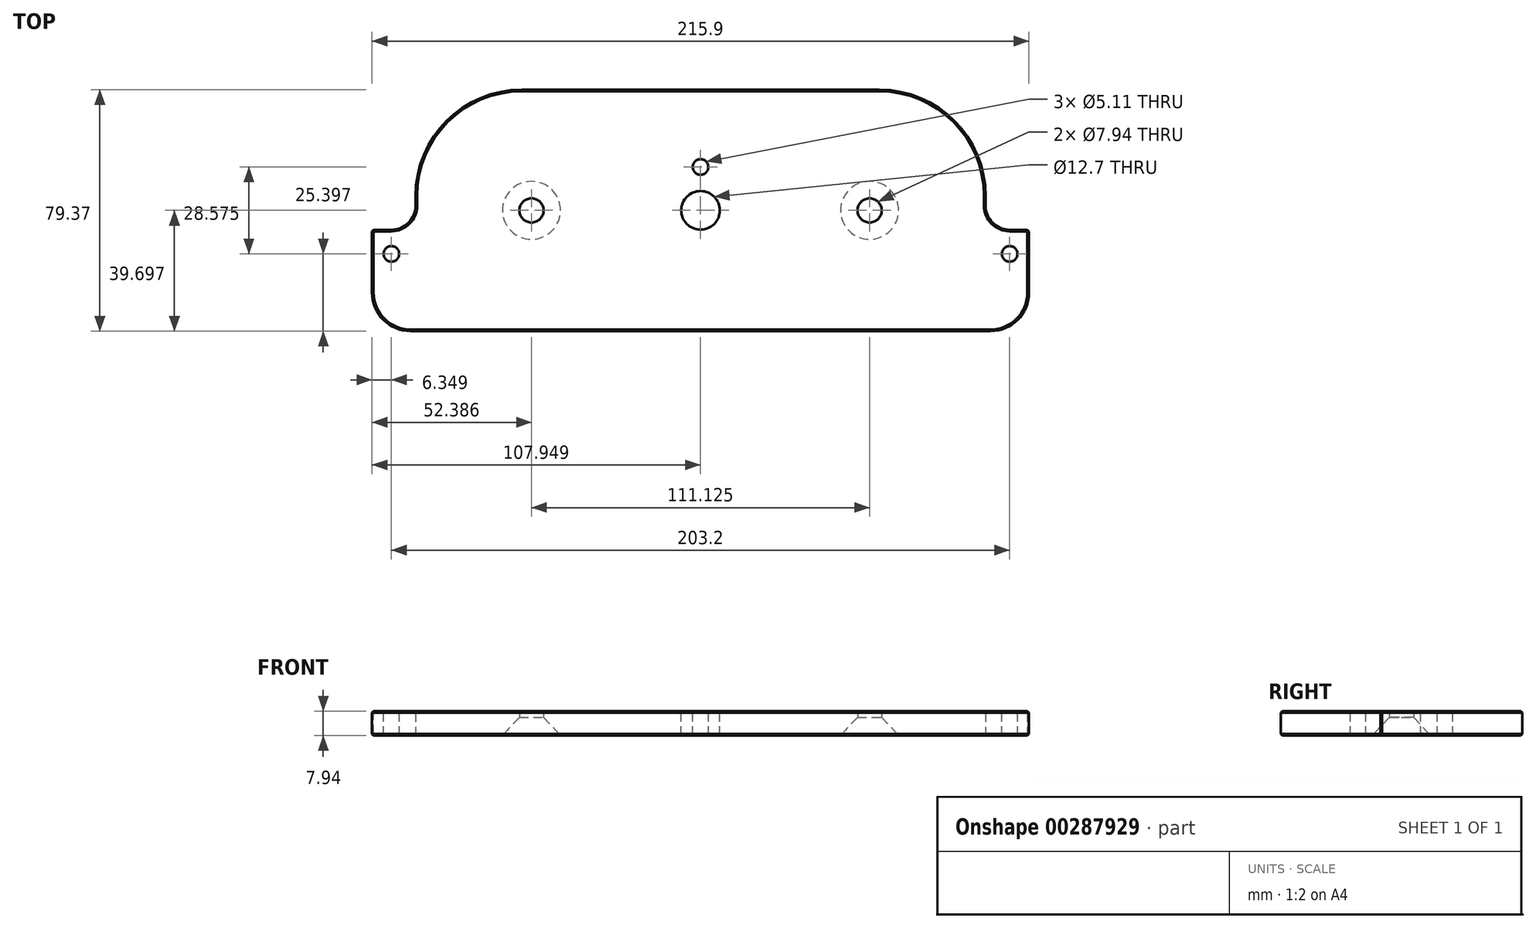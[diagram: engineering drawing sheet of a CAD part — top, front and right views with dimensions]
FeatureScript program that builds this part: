
annotation { "Feature Type Name" : "Feature", "Feature Type Description" : "" }
export const myFeature = defineFeature(function(context is Context, id is Id, definition is map)
    precondition{}
    {
        {
            var Q0;
            Q0=qCreatedBy(makeId("Top.planeOp"),FACE);
            var sketch = newSketch(context, id + "F0", { "sketchPlane" : qUnion([Q0])});
            skLineSegment(sketch, "E0.bottom", {"start": v(-112.58, 82.11) * mm, "end": v(103.32, 82.11) * mm});
            skLineSegment(sketch, "E0.top", {"start": v(-112.58, 2.74) * mm, "end": v(103.32, 2.74) * mm});
            skLineSegment(sketch, "E0.left", {"start": v(-112.58, 82.11) * mm, "end": v(-112.58, 2.74) * mm});
            skLineSegment(sketch, "E0.right", {"start": v(103.32, 82.11) * mm, "end": v(103.32, 2.74) * mm});
            skLineSegment(sketch, "E1", {"start": v(89.03, 82.11) * mm, "end": v(89.03, 36.07) * mm});
            skLineSegment(sketch, "E2", {"start": v(89.03, 36.07) * mm, "end": v(103.32, 36.07) * mm});
            skLineSegment(sketch, "E3", {"start": v(-112.58, 36.07) * mm, "end": v(-98.3, 36.07) * mm});
            skLineSegment(sketch, "E4", {"start": v(-98.3, 36.07) * mm, "end": v(-98.3, 82.11) * mm});
            skSolve(sketch);
        }
        {
            var Q0;
            {var subQ1=sQuery(id+"F0.wireOp",EDGE,"E0.top");Q0=makeQuery(id+"F0.imprint","IMPRINT",FACE,{"disambiguationData":[TD([[makeQuery(id+"F0.imprint","IMPRINT",EDGE,{"derivedFrom":subQ1}),1.0]])]});}
            extrude(context, id + "F1", {"entities" : qUnion([Q0]), "depth" : 7.94 * mm, "offsetDistance" : 25.4 * mm});
        }
        {
            var Q0;
            Q0=makeQuery(id+"F1.opExtrude","SWEPT_EDGE",EDGE,{"disambiguationData":[OSD([sQuery(id+"F0.wireOp",EDGE,"E0.top"),sQuery(id+"F0.wireOp",EDGE,"E0.left")])]});
            var Q1;
            Q1=makeQuery(id+"F1.opExtrude","SWEPT_EDGE",EDGE,{"disambiguationData":[OSD([sQuery(id+"F0.wireOp",EDGE,"E0.top"),sQuery(id+"F0.wireOp",EDGE,"E0.right")])]});
            fillet(context, id + "F2", {"entities" : qUnion([Q0, Q1]), "radius" : 12.7 * mm, "tangentPropagation" : true, "allowEdgeOverflow" : false});
        }
        {
            var Q0;
            Q0=makeQuery(id+"F1.opExtrude","SWEPT_EDGE",EDGE,{"disambiguationData":[OSD([sQuery(id+"F0.wireOp",EDGE,"E1"),sQuery(id+"F0.wireOp",EDGE,"E2")])]});
            var Q1;
            Q1=makeQuery(id+"F1.opExtrude","SWEPT_EDGE",EDGE,{"disambiguationData":[OSD([sQuery(id+"F0.wireOp",EDGE,"E3"),sQuery(id+"F0.wireOp",EDGE,"E4")])]});
            fillet(context, id + "F3", {"entities" : qUnion([Q0, Q1]), "radius" : 7.94 * mm, "tangentPropagation" : true, "allowEdgeOverflow" : false});
        }
        {
            var Q0;
            Q0=makeQuery(id+"F1.opExtrude","SWEPT_EDGE",EDGE,{"disambiguationData":[OSD([sQuery(id+"F0.wireOp",EDGE,"E0.bottom"),sQuery(id+"F0.wireOp",EDGE,"E4")])]});
            var Q1;
            Q1=makeQuery(id+"F1.opExtrude","SWEPT_EDGE",EDGE,{"disambiguationData":[OSD([sQuery(id+"F0.wireOp",EDGE,"E0.bottom"),sQuery(id+"F0.wireOp",EDGE,"E1")])]});
            fillet(context, id + "F4", {"entities" : qUnion([Q0, Q1]), "radius" : 34.92 * mm, "tangentPropagation" : true, "allowEdgeOverflow" : false});
        }
        {
            var Q0;
            Q0=makeQuery(id+"F1.opExtrude","CAP_EDGE",EDGE,{"disambiguationData":[OSD([sQuery(id+"F0.wireOp",EDGE,"E0.top")])],"isStart":false});
            var Q1;
            Q1=makeQuery(id+"F1.opExtrude","CAP_EDGE",EDGE,{"disambiguationData":[OSD([sQuery(id+"F0.wireOp",EDGE,"E0.bottom")])],"isStart":false});
            var Q2;
            Q2=makeQuery(id+"F1.opExtrude","CAP_EDGE",EDGE,{"disambiguationData":[OSD([sQuery(id+"F0.wireOp",EDGE,"E0.top")])],"isStart":true});
            var Q3;
            Q3=makeQuery(id+"F1.opExtrude","CAP_EDGE",EDGE,{"disambiguationData":[OSD([sQuery(id+"F0.wireOp",EDGE,"E0.bottom")])],"isStart":true});
            var Q4;
            Q4=makeQuery(id+"F1.opExtrude","SWEPT_EDGE",EDGE,{"disambiguationData":[OSD([sQuery(id+"F0.wireOp",EDGE,"E0.left"),sQuery(id+"F0.wireOp",EDGE,"E3")])]});
            var Q5;
            Q5=makeQuery(id+"F1.opExtrude","SWEPT_EDGE",EDGE,{"disambiguationData":[OSD([sQuery(id+"F0.wireOp",EDGE,"E0.right"),sQuery(id+"F0.wireOp",EDGE,"E2")])]});
            chamfer(context, id + "F5", {"entities" : qUnion([Q0, Q1, Q2, Q3, Q4, Q5]), "chamferType" : ChamferType.OFFSET_ANGLE, "width" : 0.5 * mm, "oppositeDirection" : false, "angle" : 45 * degree, "tangentPropagation" : true});
        }
        {
            var Q0;
            Q0=makeQuery(id+"F1.opExtrude","CAP_FACE",FACE,{"disambiguationData":[OSD([sQuery(id+"F0.wireOp",EDGE,"E0.bottom"),sQuery(id+"F0.wireOp",EDGE,"E0.top"),sQuery(id+"F0.wireOp",EDGE,"E0.left"),sQuery(id+"F0.wireOp",EDGE,"E0.right"),sQuery(id+"F0.wireOp",EDGE,"E1"),sQuery(id+"F0.wireOp",EDGE,"E2"),sQuery(id+"F0.wireOp",EDGE,"E3"),sQuery(id+"F0.wireOp",EDGE,"E4")])],"isStart":false});
            var sketch = newSketch(context, id + "F6", { "sketchPlane" : qUnion([Q0])});
            skPoint(sketch, "E5", {"position": v(-106.23, 28.14) * mm});
            skPoint(sketch, "E6", {"position": v(96.97, 28.14) * mm});
            skPoint(sketch, "E7", {"position": v(-60.2, 42.44) * mm});
            skPoint(sketch, "E8", {"position": v(50.93, 42.44) * mm});
            skPoint(sketch, "E9", {"position": v(-4.63, 42.44) * mm});
            skPoint(sketch, "E10", {"position": v(-4.63, 56.71) * mm});
            skLineSegment(sketch, "E11", {"start": v(-146.8, 28.14) * mm, "end": v(151.07, 28.14) * mm, "construction": true});
            skLineSegment(sketch, "E12", {"start": v(-144.34, 42.44) * mm, "end": v(127.48, 42.44) * mm, "construction": true});
            skLineSegment(sketch, "E13", {"start": v(-4.63, 110.64) * mm, "end": v(-4.63, -23.15) * mm, "construction": true});
            skSolve(sketch);
        }
        {
            var Q0;
            Q0=sQuery(id+"F6.wireOp",VERTEX,"E9");
            var Q1;
            Q1=makeQuery(id+"F1.opExtrude","SWEPT_BODY",BODY,{"disambiguationData":[OSD([sQuery(id+"F0.wireOp",EDGE,"E0.bottom"),sQuery(id+"F0.wireOp",EDGE,"E0.top"),sQuery(id+"F0.wireOp",EDGE,"E0.left"),sQuery(id+"F0.wireOp",EDGE,"E0.right"),sQuery(id+"F0.wireOp",EDGE,"E1"),sQuery(id+"F0.wireOp",EDGE,"E2"),sQuery(id+"F0.wireOp",EDGE,"E3"),sQuery(id+"F0.wireOp",EDGE,"E4")])]});
            hole(context, id + "F7", {"style" : HoleStyle.SIMPLE, "endStyle" : HoleEndStyle.THROUGH, "holeDiameter" : 12.7 * mm, "majorDiameter" : 6.35 * mm, "isTappedThrough" : true, "tappedDepth" : 21.59 * mm, "tapClearance" : 3, "locations" : qUnion([Q0]), "scope" : qUnion([Q1])});
        }
        {
            var Q0;
            Q0=sQuery(id+"F6.wireOp",VERTEX,"E10");
            var Q1;
            Q1=sQuery(id+"F6.wireOp",VERTEX,"E5");
            var Q2;
            Q2=sQuery(id+"F6.wireOp",VERTEX,"E6");
            var Q3;
            Q3=makeQuery(id+"F1.opExtrude","SWEPT_BODY",BODY,{"disambiguationData":[OSD([sQuery(id+"F0.wireOp",EDGE,"E0.bottom"),sQuery(id+"F0.wireOp",EDGE,"E0.top"),sQuery(id+"F0.wireOp",EDGE,"E0.left"),sQuery(id+"F0.wireOp",EDGE,"E0.right"),sQuery(id+"F0.wireOp",EDGE,"E1"),sQuery(id+"F0.wireOp",EDGE,"E2"),sQuery(id+"F0.wireOp",EDGE,"E3"),sQuery(id+"F0.wireOp",EDGE,"E4")])]});
            hole(context, id + "F8", {"style" : HoleStyle.SIMPLE, "endStyle" : HoleEndStyle.THROUGH, "standardTappedOrClearance" : lookupTablePath({ "standard" : "ANSI", "engagement" : "75%", "pitch" : "20 tpi", "size" : "1/4", "type" : "Tapped" }), "standardBlindInLast" : lookupTablePath({ "standard" : "ANSI", "engagement" : "75%", "pitch" : "20 tpi", "size" : "1/4", "type" : "Tapped" }), "holeDiameter" : 5.1 * mm, "majorDiameter" : 6.35 * mm, "showTappedDepth" : true, "isTappedThrough" : true, "tappedDepth" : 21.59 * mm, "tapClearance" : 3, "locations" : qUnion([Q0, Q1, Q2]), "scope" : qUnion([Q3])});
        }
        {
            var Q0;
            Q0=makeQuery(id+"F1.opExtrude","CAP_FACE",FACE,{"disambiguationData":[OSD([sQuery(id+"F0.wireOp",EDGE,"E0.bottom"),sQuery(id+"F0.wireOp",EDGE,"E0.top"),sQuery(id+"F0.wireOp",EDGE,"E0.left"),sQuery(id+"F0.wireOp",EDGE,"E0.right"),sQuery(id+"F0.wireOp",EDGE,"E1"),sQuery(id+"F0.wireOp",EDGE,"E2"),sQuery(id+"F0.wireOp",EDGE,"E3"),sQuery(id+"F0.wireOp",EDGE,"E4")])],"isStart":true});
            var sketch = newSketch(context, id + "F9", { "sketchPlane" : qUnion([Q0])});
            skPoint(sketch, "E14", {"position": v(50.93, -42.44) * mm});
            skPoint(sketch, "E15", {"position": v(-60.2, -42.44) * mm});
            skSolve(sketch);
        }
        {
            var Q0;
            Q0=sQuery(id+"F9.wireOp",VERTEX,"E14");
            var Q1;
            Q1=sQuery(id+"F9.wireOp",VERTEX,"E15");
            var Q2;
            Q2=makeQuery(id+"F1.opExtrude","SWEPT_BODY",BODY,{"disambiguationData":[OSD([sQuery(id+"F0.wireOp",EDGE,"E0.bottom"),sQuery(id+"F0.wireOp",EDGE,"E0.top"),sQuery(id+"F0.wireOp",EDGE,"E0.left"),sQuery(id+"F0.wireOp",EDGE,"E0.right"),sQuery(id+"F0.wireOp",EDGE,"E1"),sQuery(id+"F0.wireOp",EDGE,"E2"),sQuery(id+"F0.wireOp",EDGE,"E3"),sQuery(id+"F0.wireOp",EDGE,"E4")])]});
            hole(context, id + "F10", {"style" : HoleStyle.C_SINK, "endStyle" : HoleEndStyle.THROUGH, "holeDiameter" : 7.94 * mm, "cSinkDiameter" : 19.05 * mm, "cSinkAngle" : 86 * degree, "majorDiameter" : 6.35 * mm, "isTappedThrough" : true, "tappedDepth" : 21.59 * mm, "tapClearance" : 3, "locations" : qUnion([Q0, Q1]), "scope" : qUnion([Q2])});
        }
    });
